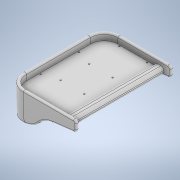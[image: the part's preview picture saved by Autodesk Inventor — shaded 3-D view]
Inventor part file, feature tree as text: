
AUTODESK INVENTOR PART (.ipt)
format: ipt  version: 2021 (Build 250183000, 183)  size: 1,212,416 bytes
history: native  units: mm
features: sketch x13, projected_geometry x9, plane x5, other x5, extrude x4, fillet x4, hole x3, loft x1, chamfer x1, mirror x1
ambient origin geometry x8: Origin, YZ Plane, XZ Plane, XY Plane, X Axis, Y Axis, Z Axis, Center Point
bodies: Body1 (feature_tree), Body2 (feature_tree), Body3 (feature_tree)
feature tree (46):
  sketch  "草圖1"
  plane  "工作平面1"
  sketch  "草圖2"
  plane  "工作平面2"
  sketch  "草圖3"
  sketch  "草圖5"
  plane  "工作平面4"
  loft  "斷面混成3"
  plane  "工作平面3"
  extrude  "擠出2"  Depth=700.0mm
  fillet  "圓角8"  Radius=500.0mm
  fillet  "圓角9"  Radius=20.0mm
  fillet  "圓角10"  Radius=20.0mm
  plane  "工作平面5"
  chamfer  "倒角2"  Distance=100.0mm
  hole  "孔1"  [1 undecoded]
  extrude  "擠出3"  [1 undecoded]
  hole  "孔2"  [1 undecoded]
  extrude  "擠出4"  [1 undecoded]
  fillet  "圓角12"  [1 undecoded]
  extrude  "擠出6"  [1 undecoded]
  mirror  "鏡射1"
  hole  "孔3"  [1 undecoded]
  sketch  "草圖6"
  other  "實體3"
  sketch  "草圖7"
  sketch  "草圖8"
  sketch  "草圖9"
  projected_geometry  "投影迴路1"
  sketch  "草圖10"
  projected_geometry  "投影迴路2"
  other  "實體4"
  sketch  "草圖11"
  projected_geometry  "投影迴路3"
  projected_geometry  "投影迴路4"
  projected_geometry  "投影迴路5"
  projected_geometry  "投影迴路6"
  projected_geometry  "投影迴路7"
  projected_geometry  "投影迴路8"
  sketch  "草圖12"
  other  "實體5"
  sketch  "草圖14"
  projected_geometry  "投影迴路10"
  sketch  "草圖15"
  other  "投影切割邊1"
  other  "投影切割邊2"
note: 7 required parameter values undecoded (feature->parameter linkage not recoverable at this tier; creation-order binding heuristic only, values carry confidence <= 0.55)
